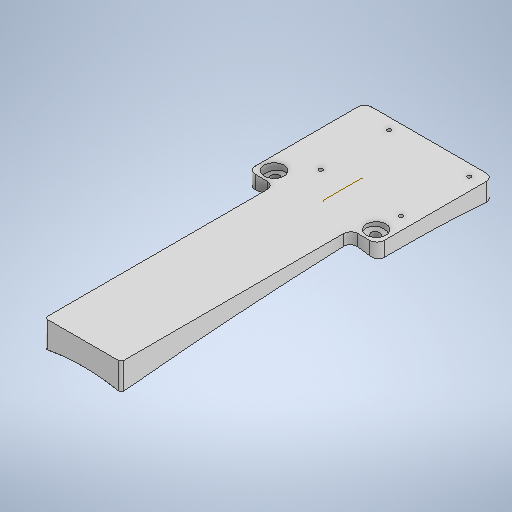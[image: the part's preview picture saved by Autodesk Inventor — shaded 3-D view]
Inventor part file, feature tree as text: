
AUTODESK INVENTOR PART (.ipt)
format: ipt  version: 2025 (Build 290162000, 162)  size: 573,440 bytes
history: native  units: in
note: dims shown in document units (in); Inventor stores cm internally (conversion verified against a paired STEP export)
features: sketch x13, extrude x10, other x4, mirror x2, loft x2, fillet x2, revolve x1, plane x1
ambient origin geometry x8: Origin, YZ Plane, XZ Plane, XY Plane, X Axis, Y Axis, Z Axis, Center Point
bodies: Solid1 (feature_tree)
feature tree (35):
  extrude  "Extrusion1"  Depth=1.5in
  revolve  "Revolution1"  [1 undecoded]
  extrude  "Extrusion2"  Depth=0.0563in
  plane  "Work Plane9"
  mirror  "Mirror1"
  extrude  "Extrusion3"  TaperAngle=90.0deg  [1 undecoded]
  mirror  "Mirror2"
  extrude  "Extrusion4"  TaperAngle=90.0deg  [1 undecoded]
  extrude  "Extrusion5"  Depth=0.6748in
  extrude  "Extrusion13"  TaperAngle=180.0deg  [1 undecoded]
  loft  "Loft4"
  extrude  "Extrusion14"  Depth=0.356in
  sketch  "Sketch21"  dims[d31=90.0deg d32=0.712in]
  extrude  "Extrusion16"  Depth=0.712in
  extrude  "Extrusion18"  Depth=2.585in
  loft  "Loft6"
  extrude  "Extrusion19"  Depth=0.08in
  fillet  "Fillet6"  Radius=2.27in
  fillet  "Fillet7"  Radius=1.93in
  sketch  "Sketch1"  dims[d2=0.25in d3=1.5in]
  sketch  "Sketch2"  dims[d4=1.0in d5=0.0in d6=0.1in]
  sketch  "Sketch3"  dims[d7=0.12in d8=0.0563in]
  sketch  "Sketch5"  dims[d9=0.2in d10=90.0deg]
  sketch  "Sketch6"  dims[d11=0.275in d12=90.0deg]
  sketch  "Sketch7"  dims[d13=0.15in d14=0.6748in]
  sketch  "Sketch8"  dims[d15=0.1in d16=180.0deg]
  sketch  "Sketch19"  dims[d17=1.0in d18=0.0in d27=-1.8228in]
  other  "Edges7"
  other  "Edges8"
  sketch  "Sketch20"  dims[d28=1.0in d29=0.0in d30=0.356in]
  sketch  "Sketch22"  dims[d33=1.0in d34=0.0in d52=2.585in]
  sketch  "Sketch25"  dims[d53=2.585in d54=0.36in]
  other  "Edges11"
  other  "Edges12"
  sketch  "Sketch26"  dims[d55=0.33in d56=0.11in d57=2.27in d58=1.93in d59=0.11in d60=0.11in d61=0.11in d62=0.2in d63=0.0in d64=0.345in d65=0.099in d66=0.099in d76=0.11in d113=0.01in d114=0.01in d115=0.01in d116=0.001in d117=0.0in d118=29.638in d119=0.0in d120=90.0deg d121=0.0in d122=90.0deg d123=0.0in d124=90.0deg d125=6.5in d126=1.08in d127=1.08in d128=0.1in d129=0.0in d130=0.51in d131=0.08in d132=0.08in d133=0.075in d134=0.075in d135=0.075in d136=90.0deg d139=0.001in d140=0.0in d156=0.036in d157=0.036in d158=0.06in d159=0.06in d160=0.06in d161=0.001in d162=0.0in d163=100.0in d164=0.0in d165=90.0deg d166=0.0in d167=90.0deg d168=0.0in d169=90.0deg d170=0.113in d171=0.113in d172=0.113in d173=0.113in d174=10.0in d175=0.0in d176=0.2in d177=0.08in d95=0.5in d96=0.0344in d97=0.5in d98=0.0344in]
note: 4 required parameter values undecoded (feature->parameter linkage not recoverable at this tier; creation-order binding heuristic only, values carry confidence <= 0.55)